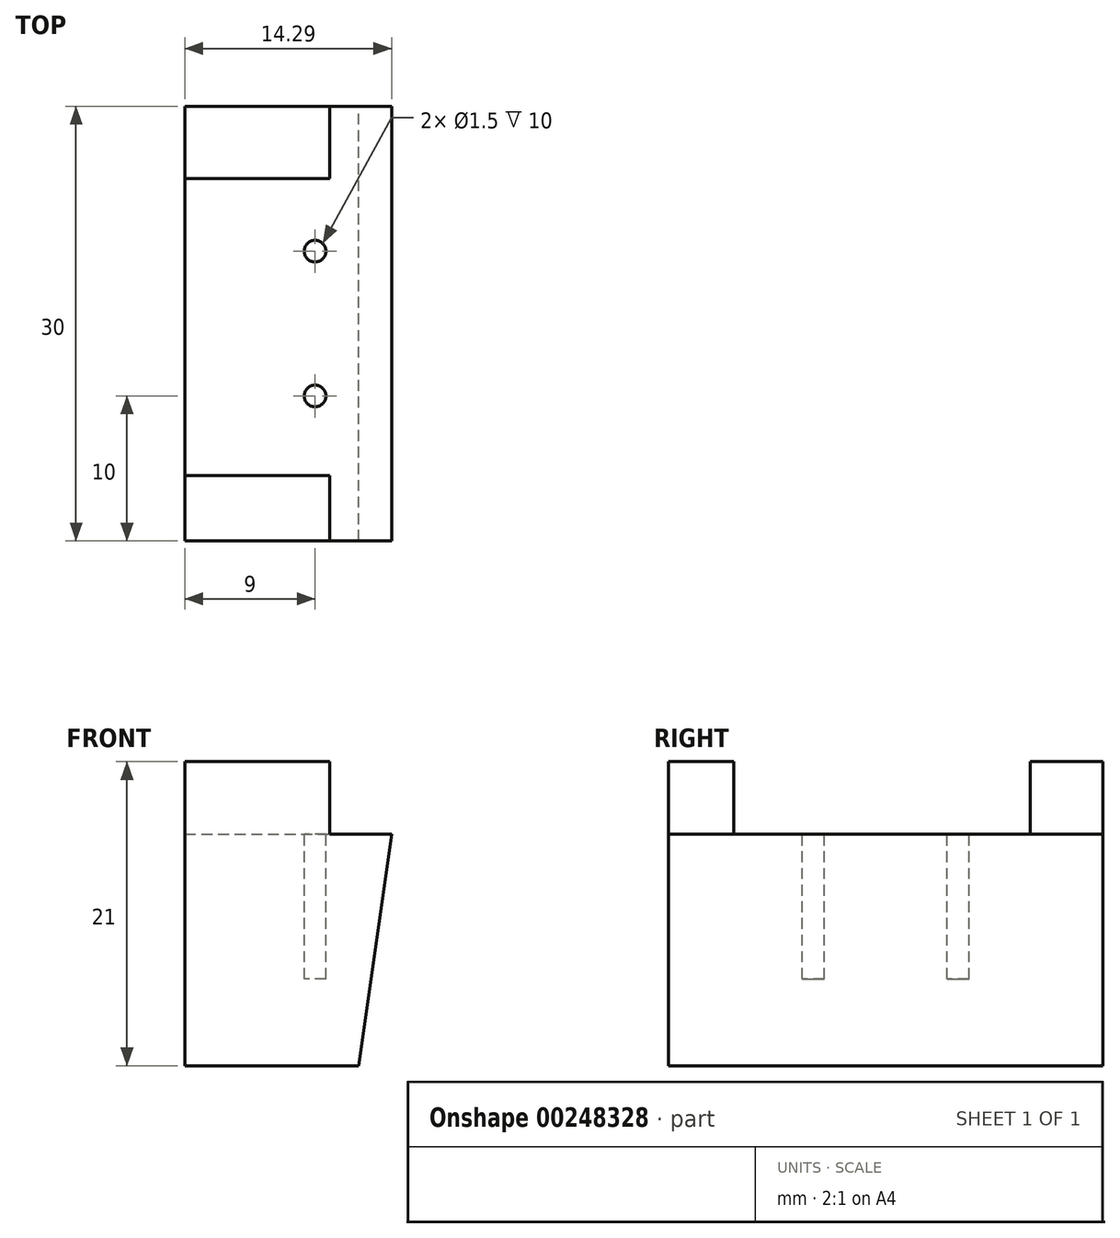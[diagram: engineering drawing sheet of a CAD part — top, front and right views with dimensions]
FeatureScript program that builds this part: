
annotation { "Feature Type Name" : "Feature", "Feature Type Description" : "" }
export const myFeature = defineFeature(function(context is Context, id is Id, definition is map)
    precondition{}
    {
        {
            var Q0;
            Q0=qCreatedBy(makeId("Front.planeOp"),FACE);
            var sketch = newSketch(context, id + "F0", { "sketchPlane" : qUnion([Q0])});
            skLineSegment(sketch, "E0", {"start": v(0, 0) * mm, "end": v(0, 16) * mm});
            skLineSegment(sketch, "E1", {"start": v(0, 16) * mm, "end": v(14.29, 16) * mm});
            skLineSegment(sketch, "E2", {"start": v(14.3, 16) * mm, "end": v(12, 0) * mm});
            skLineSegment(sketch, "E3", {"start": v(0, 0) * mm, "end": v(12, 0) * mm});
            skSolve(sketch);
        }
        {
            var Q0;
            Q0=makeQuery(id+"F0.imprint","IMPRINT",FACE,{"disambiguationData":[TD([[makeQuery(id+"F0.imprint","IMPRINT",EDGE,{"derivedFrom":sQuery(id+"F0.wireOp",EDGE,"E0")}),-1.0]])]});
            var Q1;
            Q1 = qSketchRegion(id + "F2", true);
            extrude(context, id + "F1", {"entities" : qUnion([Q0, Q1]), "depth" : 30 * mm, "offsetDistance" : 25 * mm});
        }
        {
            var Q0;
            Q0=makeQuery(id+"F1.opExtrude","SWEPT_FACE",FACE,{"disambiguationData":[OSD([sQuery(id+"F0.wireOp",EDGE,"E1")])]});
            var sketch = newSketch(context, id + "F2", { "sketchPlane" : qUnion([Q0])});
            skLineSegment(sketch, "E4", {"start": v(9, 0) * mm, "end": v(9, -30) * mm, "construction": true});
            skLineSegment(sketch, "E5", {"start": v(0, -10) * mm, "end": v(14.29, -10) * mm, "construction": true});
            skLineSegment(sketch, "E6", {"start": v(0, -20) * mm, "end": v(14.29, -20) * mm, "construction": true});
            skCircle(sketch, "E7", {"center": v(9, -10) * mm, "radius": 0.75 * mm});
            skCircle(sketch, "E8", {"center": v(9, -20) * mm, "radius": 0.75 * mm});
            skSolve(sketch);
        }
        {
            var Q0;
            Q0=makeQuery(id+"F2.imprint","IMPRINT",FACE,{"disambiguationData":[TD([[makeQuery(id+"F2.imprint","IMPRINT",EDGE,{"derivedFrom":sQuery(id+"F2.wireOp",EDGE,"E7")}),1.0]])]});
            var Q1;
            Q1=makeQuery(id+"F2.imprint","IMPRINT",FACE,{"disambiguationData":[TD([[makeQuery(id+"F2.imprint","IMPRINT",EDGE,{"derivedFrom":sQuery(id+"F2.wireOp",EDGE,"E8")}),1.0]])]});
            extrude(context, id + "F3", {"entities" : qUnion([Q0, Q1]), "operationType" : NewBodyOperationType.REMOVE, "oppositeDirection" : true, "depth" : 10 * mm, "offsetDistance" : 25 * mm});
        }
        {
            var Q0;
            Q0=makeQuery(id+"F1.opExtrude","SWEPT_FACE",FACE,{"disambiguationData":[OSD([sQuery(id+"F0.wireOp",EDGE,"E1")])]});
            var sketch = newSketch(context, id + "F4", { "sketchPlane" : qUnion([Q0])});
            skLineSegment(sketch, "E9", {"start": v(0, -5) * mm, "end": v(10, -5) * mm});
            skLineSegment(sketch, "E10", {"start": v(0, -25.5) * mm, "end": v(10, -25.5) * mm});
            skLineSegment(sketch, "E11", {"start": v(10, 0) * mm, "end": v(10, -5) * mm});
            skPoint(sketch, "E12.orphan", {"position": v(14.29, -5) * mm});
            skLineSegment(sketch, "E13.trimOffspring", {"start": v(10, -25.5) * mm, "end": v(10, -30) * mm});
            skPoint(sketch, "E14.orphan", {"position": v(14.29, -25.5) * mm});
            skSolve(sketch);
        }
        {
            var Q0;
            {var subQ0=sQuery(id+"F4.wireOp",EDGE,"E9");Q0=makeQuery(id+"F4.imprint","IMPRINT",FACE,{"disambiguationData":[TD([[makeQuery(id+"F4.imprint","IMPRINT",EDGE,{"derivedFrom":subQ0}),1.0]])]});}
            var Q1;
            {var subQ0=sQuery(id+"F4.wireOp",EDGE,"E10");Q1=makeQuery(id+"F4.imprint","IMPRINT",FACE,{"disambiguationData":[TD([[makeQuery(id+"F4.imprint","IMPRINT",EDGE,{"derivedFrom":subQ0}),-1.0]])]});}
            extrude(context, id + "F5", {"entities" : qUnion([Q0, Q1]), "operationType" : NewBodyOperationType.ADD, "depth" : 5 * mm, "offsetDistance" : 25 * mm});
        }
    });
